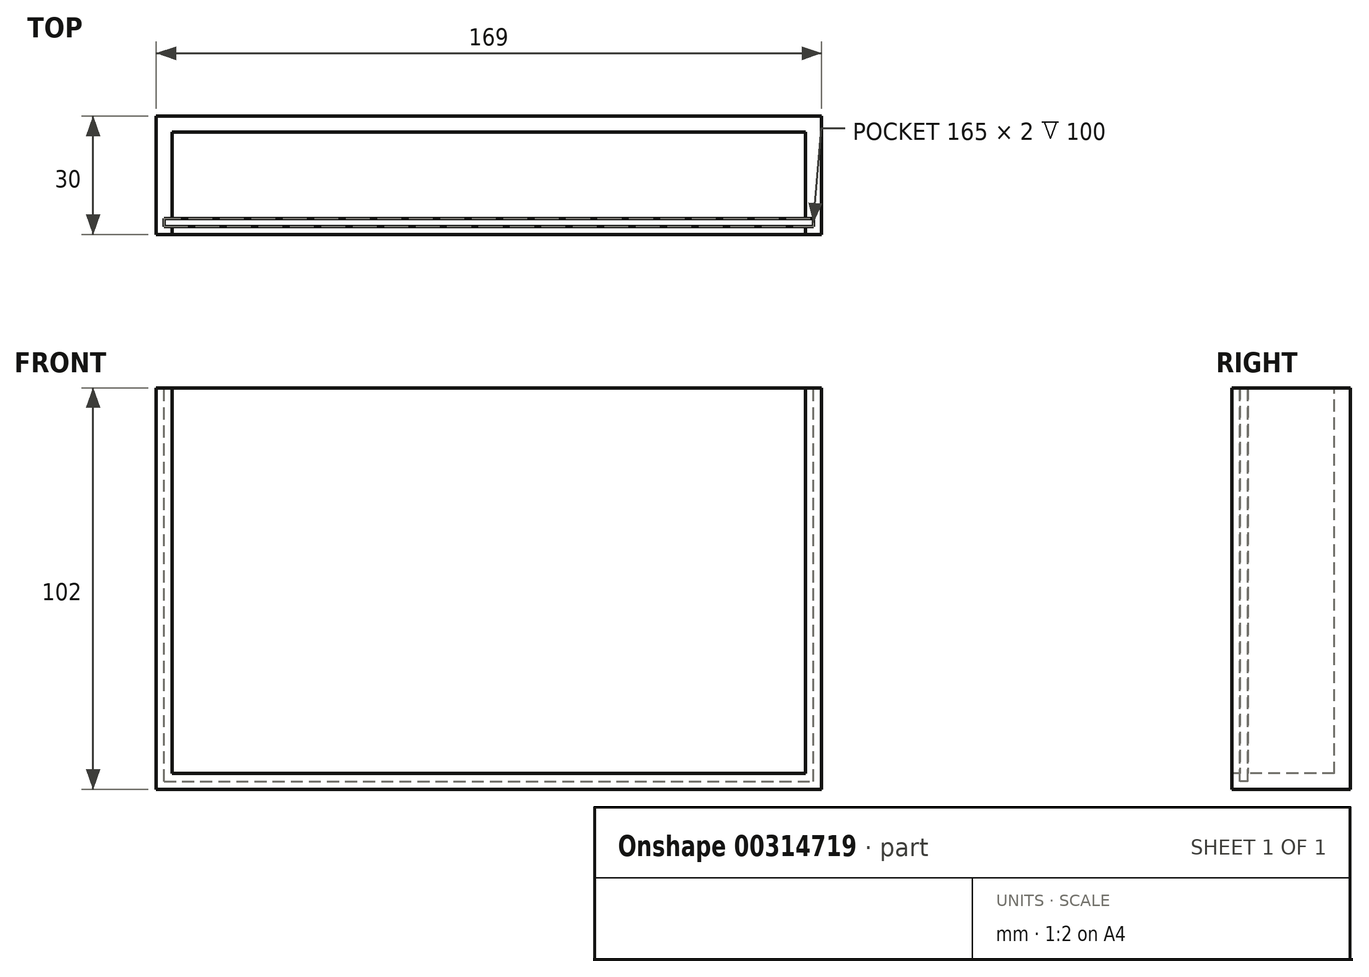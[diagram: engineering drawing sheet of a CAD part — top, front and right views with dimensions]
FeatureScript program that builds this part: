
annotation { "Feature Type Name" : "Feature", "Feature Type Description" : "" }
export const myFeature = defineFeature(function(context is Context, id is Id, definition is map)
    precondition{}
    {
        {
            assignVariable(context, id + "F0", {"name" : "shell", "anyValue" : 4});
        }
        {
            var Q0;
            Q0=qCreatedBy(makeId("Front.planeOp"),FACE);
            var sketch = newSketch(context, id + "F1", { "sketchPlane" : qUnion([Q0])});
            skLineSegment(sketch, "E0.bottom", {"start": v(82.5, -50) * mm, "end": v(-82.5, -50) * mm});
            skLineSegment(sketch, "E0.top", {"start": v(82.5, 50) * mm, "end": v(-82.5, 50) * mm});
            skLineSegment(sketch, "E0.left", {"start": v(82.5, -50) * mm, "end": v(82.5, 50) * mm});
            skLineSegment(sketch, "E0.right", {"start": v(-82.5, -50) * mm, "end": v(-82.5, 50) * mm});
            skPoint(sketch, "E0.middle", {"position": v(0, 0) * mm});
            skLineSegment(sketch, "E1.1", {"start": v(84.5, -52) * mm, "end": v(84.5, 50) * mm});
            skLineSegment(sketch, "E1.2", {"start": v(84.5, -52) * mm, "end": v(-84.5, -52) * mm});
            skLineSegment(sketch, "E1.3", {"start": v(-84.5, -52) * mm, "end": v(-84.5, 50) * mm});
            skLineSegment(sketch, "E2.0", {"start": v(80.5, 48) * mm, "end": v(-80.5, 48) * mm});
            skLineSegment(sketch, "E2.1", {"start": v(80.5, -48) * mm, "end": v(80.5, 48) * mm});
            skLineSegment(sketch, "E2.2", {"start": v(80.5, -48) * mm, "end": v(-80.5, -48) * mm});
            skLineSegment(sketch, "E2.3", {"start": v(-80.5, -48) * mm, "end": v(-80.5, 48) * mm});
            skLineSegment(sketch, "E3", {"start": v(-80.5, 48) * mm, "end": v(-80.5, 50) * mm});
            skLineSegment(sketch, "E4", {"start": v(80.5, 48) * mm, "end": v(80.5, 50) * mm});
            skLineSegment(sketch, "E5", {"start": v(82.5, 50) * mm, "end": v(84.5, 50) * mm});
            skLineSegment(sketch, "E6", {"start": v(-82.5, 50) * mm, "end": v(-84.5, 50) * mm});
            skSolve(sketch);
        }
        {
            var Q0;
            Q0=makeQuery(id+"F1.imprint","IMPRINT",FACE,{"disambiguationData":[TD([[makeQuery(id+"F1.imprint","IMPRINT",EDGE,{"derivedFrom":sQuery(id+"F1.wireOp",EDGE,"E0.bottom")}),1.0]])]});
            var Q1;
            Q1=makeQuery(id+"F1.imprint","IMPRINT",FACE,{"disambiguationData":[TD([[makeQuery(id+"F1.imprint","IMPRINT",EDGE,{"derivedFrom":sQuery(id+"F1.wireOp",EDGE,"E0.bottom")}),-1.0]])]});
            var Q2;
            Q2=makeQuery(id+"F1.imprint","IMPRINT",FACE,{"disambiguationData":[TD([[makeQuery(id+"F1.imprint","IMPRINT",EDGE,{"derivedFrom":sQuery(id+"F1.wireOp",EDGE,"E2.0")}),1.0]])]});
            var Q3;
            Q3=makeQuery(id+"F1.imprint","IMPRINT",FACE,{"disambiguationData":[TD([[makeQuery(id+"F1.imprint","IMPRINT",EDGE,{"derivedFrom":sQuery(id+"F1.wireOp",EDGE,"E2.0")}),-1.0]])]});
            extrude(context, id + "F2", {"entities" : qUnion([Q0, Q1, Q2, Q3]), "depth" : -30 * mm});
        }
        {
            var Q0;
            Q0=makeQuery(id+"F2.opExtrude","SWEPT_FACE",FACE,{"disambiguationData":[OSD([sQuery(id+"F1.wireOp",EDGE,"E0.top"),sQuery(id+"F1.wireOp",EDGE,"E5"),sQuery(id+"F1.wireOp",EDGE,"E6")])]});
            var Q1;
            Q1=makeQuery(id+"F2.opExtrude","CAP_FACE",FACE,{"disambiguationData":[OSD([sQuery(id+"F1.wireOp",EDGE,"E0.top"),sQuery(id+"F1.wireOp",EDGE,"E1.1"),sQuery(id+"F1.wireOp",EDGE,"E1.2"),sQuery(id+"F1.wireOp",EDGE,"E1.3"),sQuery(id+"F1.wireOp",EDGE,"E5"),sQuery(id+"F1.wireOp",EDGE,"E6")])],"isStart":true});
            shell(context, id + "F3", {"entities" : qUnion([Q0, Q1]), "thickness" : (getVariable(context, 'shell')) * mm});
        }
        {
            var Q0;
            Q0=makeQuery(id+"F2.opExtrude","SWEPT_FACE",FACE,{"disambiguationData":[OSD([sQuery(id+"F1.wireOp",EDGE,"E0.top"),sQuery(id+"F1.wireOp",EDGE,"E5"),sQuery(id+"F1.wireOp",EDGE,"E6")])]});
            var sketch = newSketch(context, id + "F4", { "sketchPlane" : qUnion([Q0])});
            skLineSegment(sketch, "E7.0.0", {"start": v(-80.5, 26) * mm, "end": v(80.5, 26) * mm});
            skLineSegment(sketch, "E7.0.1", {"start": v(80.5, 26) * mm, "end": v(80.5, 0) * mm});
            skLineSegment(sketch, "E7.0.2", {"start": v(80.5, 0) * mm, "end": v(84.5, 0) * mm});
            skLineSegment(sketch, "E7.0.3", {"start": v(84.5, 0) * mm, "end": v(84.5, 30) * mm});
            skLineSegment(sketch, "E7.0.4", {"start": v(84.5, 30) * mm, "end": v(-84.5, 30) * mm});
            skLineSegment(sketch, "E7.0.5", {"start": v(-84.5, 30) * mm, "end": v(-84.5, 0) * mm});
            skLineSegment(sketch, "E7.0.6", {"start": v(-84.5, 0) * mm, "end": v(-80.5, 0) * mm});
            skLineSegment(sketch, "E7.0.7", {"start": v(-80.5, 0) * mm, "end": v(-80.5, 26) * mm});
            skLineSegment(sketch, "E8", {"start": v(-82.5, 0) * mm, "end": v(-82.5, 30) * mm, "construction": true});
            skLineSegment(sketch, "E9", {"start": v(82.5, 0) * mm, "end": v(82.5, 30) * mm, "construction": true});
            skLineSegment(sketch, "E10.bottom", {"start": v(-82.5, 4) * mm, "end": v(82.5, 4) * mm});
            skLineSegment(sketch, "E10.top", {"start": v(-82.5, 2) * mm, "end": v(82.5, 2) * mm});
            skLineSegment(sketch, "E10.left", {"start": v(-82.5, 4) * mm, "end": v(-82.5, 2) * mm, "construction": true});
            skLineSegment(sketch, "E10.right", {"start": v(82.5, 4) * mm, "end": v(82.5, 2) * mm, "construction": true});
            skLineSegment(sketch, "E11", {"start": v(-82.5, 4) * mm, "end": v(-82.5, 2) * mm});
            skLineSegment(sketch, "E12", {"start": v(82.5, 4) * mm, "end": v(82.5, 2) * mm});
            skSolve(sketch);
        }
        {
            var Q0;
            {var subQ0=sQuery(id+"F4.wireOp",EDGE,"E10.top");var subQ1=sQuery(id+"F4.wireOp",EDGE,"E7.0.1");var subQ2=makeQuery(id+"F4.imprint","INTERSECT",VERTEX,{"derivedFrom":[subQ1,subQ0]});Q0=makeQuery(id+"F4.imprint","IMPRINT",FACE,{"disambiguationData":[TD([[makeQuery(id+"F4.imprint","IMPRINT",EDGE,{"disambiguationData":[TD([[subQ2,1.0]])],"derivedFrom":subQ1}),-1.0]])]});}
            var Q1;
            {var subQ5=sQuery(id+"F4.wireOp",EDGE,"E11");Q1=makeQuery(id+"F4.imprint","IMPRINT",FACE,{"disambiguationData":[TD([[makeQuery(id+"F4.imprint","IMPRINT",EDGE,{"derivedFrom":subQ5}),1.0]])]});}
            var Q2;
            {var subQ5=sQuery(id+"F4.wireOp",EDGE,"E12");Q2=makeQuery(id+"F4.imprint","IMPRINT",FACE,{"disambiguationData":[TD([[makeQuery(id+"F4.imprint","IMPRINT",EDGE,{"derivedFrom":subQ5}),-1.0]])]});}
            extrude(context, id + "F5", {"entities" : qUnion([Q0, Q1, Q2]), "operationType" : NewBodyOperationType.REMOVE, "oppositeDirection" : true, "depth" : 100 * mm});
        }
    });
